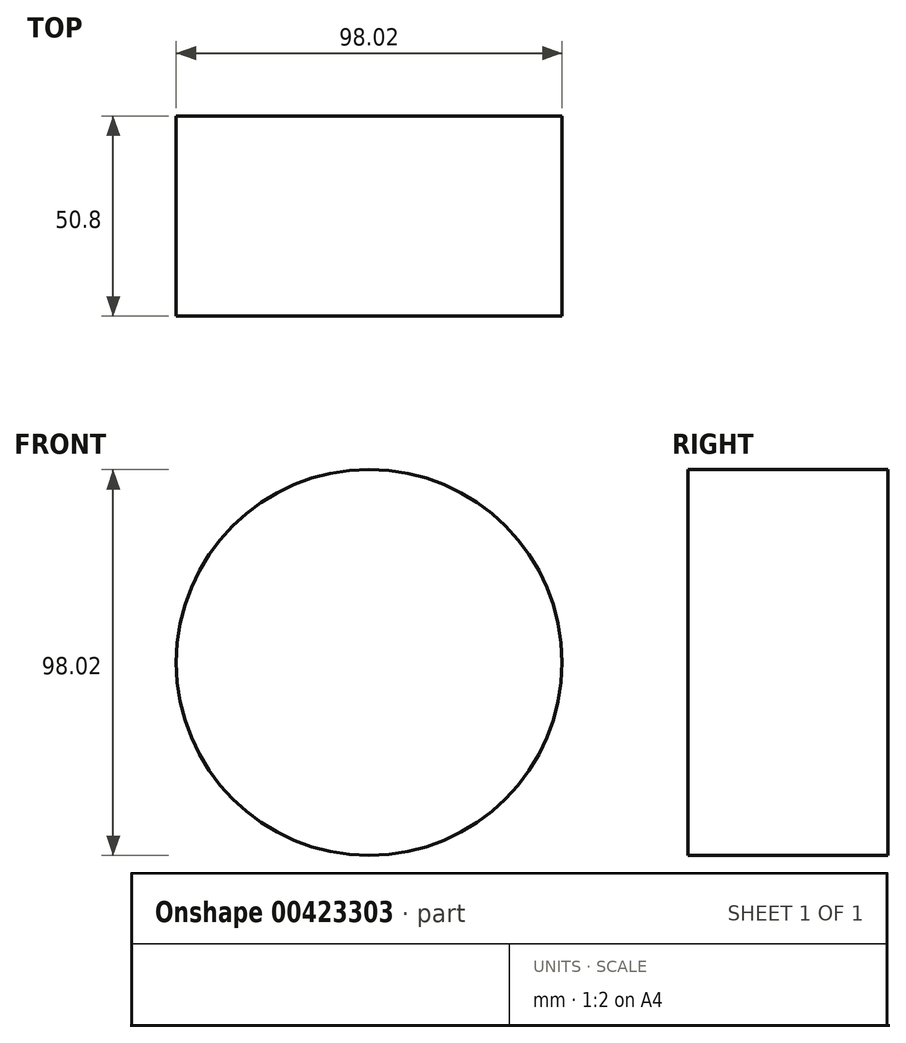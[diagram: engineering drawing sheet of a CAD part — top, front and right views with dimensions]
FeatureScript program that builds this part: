
annotation { "Feature Type Name" : "Feature", "Feature Type Description" : "" }
export const myFeature = defineFeature(function(context is Context, id is Id, definition is map)
    precondition{}
    {
        {
            var Q0;
            Q0=qCreatedBy(makeId("Front.planeOp"),FACE);
            var sketch = newSketch(context, id + "F0", { "sketchPlane" : qUnion([Q0])});
            skCircle(sketch, "E0", {"center": v(11.65, 0) * mm, "radius": 46.37 * mm});
            skCircle(sketch, "E1", {"center": v(0, 32.53) * mm, "radius": 48.78 * mm});
            skCircle(sketch, "E2", {"center": v(-26.02, -8.73) * mm, "radius": 48.78 * mm});
            skCircle(sketch, "E3", {"center": v(10.34, 23.8) * mm, "radius": 128.81 * mm});
            skSolve(sketch);
        }
        {
            var Q0;
            Q0 = qSketchRegion(id + "F0", true);
            extrude(context, id + "F1", {"entities" : qUnion([Q0]), "depth" : 25.4 * mm});
        }
        {
            var Q0;
            Q0=makeQuery(id+"F1.opExtrude","SWEPT_BODY",BODY,{"disambiguationData":[OSD([sQuery(id+"F0.wireOp",EDGE,"E0"),sQuery(id+"F0.wireOp",EDGE,"E1"),sQuery(id+"F0.wireOp",EDGE,"E2"),sQuery(id+"F0.wireOp",EDGE,"E3")])]});
            deleteBodies(context, id + "F2", {"entities" : qUnion([Q0])});
        }
        {
            var Q0;
            Q0=qCreatedBy(makeId("Front.planeOp"),FACE);
            var sketch = newSketch(context, id + "F3", { "sketchPlane" : qUnion([Q0])});
            skCircle(sketch, "E4", {"center": v(0, 0) * mm, "radius": 49.01 * mm});
            skSolve(sketch);
        }
        {
            var Q0;
            Q0 = qSketchRegion(id + "F3", true);
            extrude(context, id + "F4", {"entities" : qUnion([Q0]), "depth" : 50.8 * mm});
        }
        {
            var Q0;
            Q0=qCreatedBy(makeId("Front.planeOp"),FACE);
            var sketch = newSketch(context, id + "F5", { "sketchPlane" : qUnion([Q0])});
            skCircle(sketch, "E5", {"center": v(0, 0) * mm, "radius": 33.61 * mm});
            skSolve(sketch);
        }
        {
            var Q0;
            Q0=sQuery(id+"F5.wireOp",EDGE,"E5");
            extrude(context, id + "F6", {"bodyType" : ToolBodyType.SURFACE, "surfaceEntities" : qUnion([Q0]), "depth" : 50.8 * mm});
        }
    });
